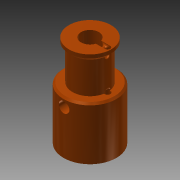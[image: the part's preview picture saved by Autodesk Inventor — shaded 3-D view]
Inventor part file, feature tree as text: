
AUTODESK INVENTOR PART (.ipt)
format: ipt  version: 2013 (Build 170138000, 138)  size: 335,360 bytes
history: native  units: mm
features: sketch x12, extrude x10, fillet x5, chamfer x2, revolve x2
ambient origin geometry x8: Origin, YZ Plane, XZ Plane, XY Plane, X Axis, Y Axis, Z Axis, Center Point
bodies: Solid1 (feature_tree)
feature tree (31):
  extrude  "Extrusion1"  Depth=15.0mm TaperAngle=0.0deg
  extrude  "Extrusion2"  Depth=11.0mm TaperAngle=0.0deg
  extrude  "Extrusion3"  Depth=2.0mm TaperAngle=0.0deg
  chamfer  "Chamfer1"  Distance=1.0mm Angle=45.0deg
  extrude  "Extrusion4"  Depth=2.0mm TaperAngle=0.0deg
  revolve  "Revolution1"  [1 undecoded]
  extrude  "Extrusion5"  Depth=5.1mm
  revolve  "Revolution2"  [1 undecoded]
  extrude  "Extrusion6"  Depth=15.0mm TaperAngle=0.0deg
  extrude  "Extrusion7"  Depth=1.5mm
  chamfer  "Chamfer2"  Distance=15.0mm
  extrude  "Extrusion8"  Depth=0.49mm
  extrude  "Extrusion9"  Depth=0.5mm TaperAngle=0.0deg
  fillet  "Fillet1"  Radius=0.49mm
  fillet  "Fillet2"  Radius=0.49mm
  extrude  "Extrusion10"  [1 undecoded]
  fillet  "Fillet3"  [1 undecoded]
  fillet  "Fillet4"  [1 undecoded]
  fillet  "Fillet5"  [1 undecoded]
  sketch  "Sketch1"  dims[d0=15.0mm d2=15.0mm d3=0.0mm]
  sketch  "Sketch2"  dims[d4=10.0mm d6=11.0mm d7=0.0mm]
  sketch  "Sketch3"  dims[d8=1.0mm d9=2.0mm d10=0.0mm d11=1.0mm d12=2.0mm d13=45.0deg]
  sketch  "Sketch4"  dims[d14=1.5mm d16=2.0mm d17=0.0mm]
  sketch  "Sketch5"  dims[d18=90.0deg d19=15.0mm d20=0.0mm]
  sketch  "Sketch6"  dims[d21=90.0deg d22=5.1mm]
  sketch  "Sketch7"  dims[d27=15.0mm d28=0.0mm d29=12.5mm]
  sketch  "Sketch8"  dims[d30=3.0mm d31=15.0mm d32=0.0mm]
  sketch  "Sketch9"  dims[d33=0.5mm d34=2.0mm d35=45.0deg d36=1.5mm d39=15.0mm d40=0.0mm]
  sketch  "Sketch10"  dims[d41=0.5mm d42=0.0mm d43=0.49mm]
  sketch  "Sketch11"  dims[d44=0.49mm d45=0.5mm d46=0.0mm d47=0.49mm d48=0.49mm]
  sketch  "Sketch12"  dims[d49=0.25mm]
note: 6 required parameter values undecoded (feature->parameter linkage not recoverable at this tier; creation-order binding heuristic only, values carry confidence <= 0.55)